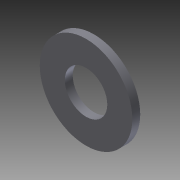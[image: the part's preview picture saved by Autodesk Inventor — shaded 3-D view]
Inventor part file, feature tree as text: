
AUTODESK INVENTOR PART (.ipt)
format: ipt  version: 2013 (Build 170138000, 138)  size: 73,216 bytes
history: native  units: mm (DEFAULTED — no unit token found)
features: extrude x1, sketch x1
ambient origin geometry x8: Origin, YZ Plane, XZ Plane, XY Plane, X Axis, Y Axis, Z Axis, Center Point
bodies: Solid1 (feature_tree)
feature tree (2):
  extrude  "Extrusion1"  Depth=4.3688mm
  sketch  "Sketch1"  dims[d0=9.525mm d1=4.3688mm d2=0.8128mm d3=0.0mm]
